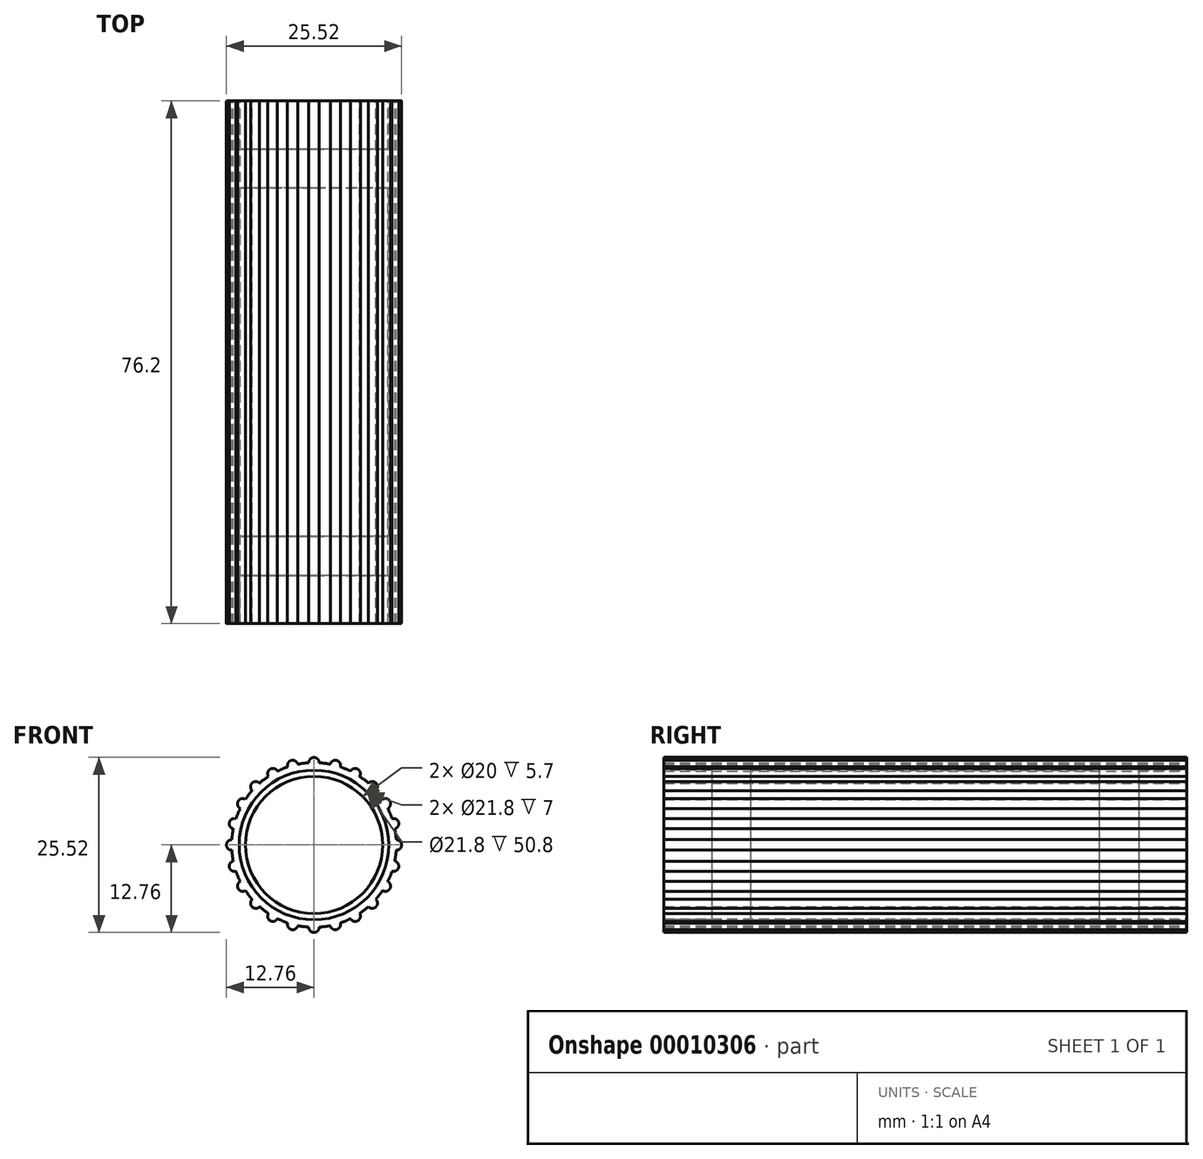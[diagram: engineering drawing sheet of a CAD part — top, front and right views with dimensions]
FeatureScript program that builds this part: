
annotation { "Feature Type Name" : "Feature", "Feature Type Description" : "" }
export const myFeature = defineFeature(function(context is Context, id is Id, definition is map)
    precondition{}
    {
        {
            var Q0;
            Q0=qCreatedBy(makeId("Front.planeOp"),FACE);
            var sketch = newSketch(context, id + "F0", { "sketchPlane" : qUnion([Q0])});
            skCircle(sketch, "E0", {"center": v(0, 0) * mm, "radius": 10 * mm});
            skCircle(sketch, "E1", {"center": v(0, 0) * mm, "radius": 12 * mm});
            skSolve(sketch);
        }
        {
            var Q0;
            Q0 = qSketchRegion(id + "F0", true);
            extrude(context, id + "F1", {"entities" : qUnion([Q0]), "endBound" : BoundingType.SYMMETRIC, "depth" : 76.2 * mm});
        }
        {
            var Q0;
            Q0=makeQuery(id+"F1.opExtrude","CAP_FACE",FACE,{"disambiguationData":[OSD([sQuery(id+"F0.wireOp",EDGE,"E0"),sQuery(id+"F0.wireOp",EDGE,"E1")])],"isStart":false});
            var sketch = newSketch(context, id + "F2", { "sketchPlane" : qUnion([Q0])});
            skCircle(sketch, "E2", {"center": v(0, 0) * mm, "radius": 10.9 * mm});
            skSolve(sketch);
        }
        {
            var Q0;
            Q0 = qSketchRegion(id + "F2", true);
            extrude(context, id + "F3", {"entities" : qUnion([Q0]), "operationType" : NewBodyOperationType.REMOVE, "oppositeDirection" : true, "depth" : 7 * mm});
        }
        {
            var Q0;
            Q0=makeQuery(id+"F1.opExtrude","CAP_FACE",FACE,{"disambiguationData":[OSD([sQuery(id+"F0.wireOp",EDGE,"E0"),sQuery(id+"F0.wireOp",EDGE,"E1")])],"isStart":true});
            var sketch = newSketch(context, id + "F4", { "sketchPlane" : qUnion([Q0])});
            skCircle(sketch, "E3", {"center": v(0, 0) * mm, "radius": 10.9 * mm});
            skSolve(sketch);
        }
        {
            var Q0;
            Q0 = qSketchRegion(id + "F4", true);
            extrude(context, id + "F5", {"entities" : qUnion([Q0]), "operationType" : NewBodyOperationType.REMOVE, "oppositeDirection" : true, "depth" : 7 * mm});
        }
        {
            var Q0;
            Q0=qCreatedBy(makeId("Front.planeOp"),FACE);
            var sketch = newSketch(context, id + "F6", { "sketchPlane" : qUnion([Q0])});
            skCircle(sketch, "E4", {"center": v(0, 0) * mm, "radius": 10.9 * mm});
            skSolve(sketch);
        }
        {
            var Q0;
            Q0 = qSketchRegion(id + "F6", true);
            extrude(context, id + "F7", {"entities" : qUnion([Q0]), "operationType" : NewBodyOperationType.REMOVE, "endBound" : BoundingType.SYMMETRIC, "depth" : 50.8 * mm});
        }
        {
            var Q0;
            Q0=qCreatedBy(makeId("Front.planeOp"),FACE);
            var sketch = newSketch(context, id + "F8", { "sketchPlane" : qUnion([Q0])});
            skCircle(sketch, "E5", {"center": v(0, 12) * mm, "radius": 0.76 * mm});
            skSolve(sketch);
        }
        {
            var Q0;
            Q0 = qSketchRegion(id + "F8", true);
            extrude(context, id + "F9", {"entities" : qUnion([Q0]), "operationType" : NewBodyOperationType.ADD, "endBound" : BoundingType.SYMMETRIC, "depth" : 76.2 * mm});
        }
        {
            var Q0;
            Q0=makeQuery(id+"F9.opExtrude","SWEPT_FACE",FACE,{"disambiguationData":[OSD([sQuery(id+"F8.wireOp",EDGE,"E5")])]});
            var Q1;
            Q1=makeQuery(id+"F1.opExtrude","CAP_EDGE",EDGE,{"disambiguationData":[OSD([sQuery(id+"F0.wireOp",EDGE,"E1")])],"isStart":false});
            circularPattern(context, id + "F10", {"faces" : qUnion([Q0]), "axis" : qUnion([Q1]), "angle" : 15 * degree, "instanceCount" : 24, "patternType" : PatternType.FACE});
        }
    });
